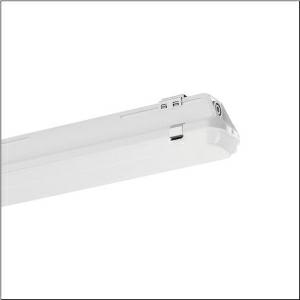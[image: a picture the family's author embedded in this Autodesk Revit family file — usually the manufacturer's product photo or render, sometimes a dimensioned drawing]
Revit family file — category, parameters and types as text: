
# Revit family: monsun_r__12_51fp30mp480h_d9a5
name_source: partatom
category: Lighting Fixtures
units: mm (PartAtom-declared; Revit-internal decimal feet)

## family parameters
Cut with Voids When Loaded = No
Host = Face
Light Source = No
Part Type = Normal
Room Calculation Point = No
Round Connector Dimension = Use Diameter
Shared = No

## types (1)
- --- (1 x LED, 7640 lm, 45.4 W, 4000K)
    Apparent Load = 45 VA
    CIE Flux Codes = 48 77 93 95 100
    Color Rendering = 80
    Color Temperature = 4000K
    Default Elevation = 1800 mm
    Description = Monsun® 12, damp-proof luminaire, chain hanger, primary optical cover: enclosure, of PA, light emission: direct distribution, primary light characteristic: symmetric, installation type: suspended mounting, surface-mounted, horizontal mounting, vertical mounting, LED rated luminous flux: 7.640 lm, light colour: 840, colour temperature: 4000K, control gear: ECG, with terminal, 3-pole, max. 2.5mm², mains connection: 220..240V, AC, 50/60Hz, rated input power: 45W, luminaire housing, of glass-fibre reinforced polyester, uncoated, bright grey, length: 1.590 mm, width: 90 mm, height: 88mm, clip for enclosure, of stainless steel (V2A), ceiling mounting element, of stainless steel (V2A), chain hanger, of stainless steel (V2A), protection rating (complete): IP66, insulation class (complete): insulation class I (protective earthing), certification: CE, ENEC, VDE, protection symbol: D, impact resistance: IK08, permissible ambient temperature for indoor applications: -35..+40°C, standard: EN 50419, EN 60598-2-1, no direct snow, no direct sun, no direct rain, for indoor or canopied outdoor use, corresponds to IFS (International Featured Standards) requirements for safety and quality in the food industry, packaging unit: 1 piece
    Height = 89 mm
    Lamp = 1 x LED
    Lamp Light Flux = 7640 lm
    Lamp Power = 45.4 W
    Lamp count = 1
    Length = 1590 mm
    Luminous efficacy = 168 lm/W
    Manufacturer = Siteco
    ModVariant = No
    Model = 51FP30MP480H
    Mounting Place = Ceiling
    Mounting Type = Pendant
    Number of Poles = 1
    OnlyDefault = Yes
    Power Factor = 1
    Product Name = Monsun® 12
    Product group = damp-proof luminaire | ceiling pendant
    ProductGroupID = 908
    Protection Class = Protection class I
    Protection Degree = IP 66
    RLX_Detail_Level = 1
    RlxData = <blob elided: 89461 chars, md5=a5166f3b>
    Socket = socket
    Standby Power = 0 W
    System Light Flux = 7640 lm
    System Power = 45 W
    Type Comments = factory setting: luminous flux: 100 % | (A | C | E) | 105 mA
    Type Image = l_1004748.jpg
    URL = http://relux.com
    VarID = @adj_136155
    Voltage = 0 V
    Weight = 0.00 kg
    Width = 90 mm

## geometry (parser evidence)
native form markers: Blend x4, Sweep x14
no freeform markers — native parametric forms only
